# Revit family: FU_Inspec_Grade_2-3
name_source: partatom
category: Furniture
units: mm (PartAtom-declared; Revit-internal decimal feet)

## family parameters
Always vertical = Yes
Cut with Voids When Loaded = No
OmniClass Number = 23.40.20.00
OmniClass Title = General Furniture and Specialties
Room Calculation Point = No
Shared = No
Work Plane-Based = No

## types (3) — shared parameters
Assembly Code = E2020
Depth = 780 mm
Frame Material = Metal - Chrome - Polished
Height = 540 mm
Keynote = 46.B
Manufacturer = Inspec
Seat Material = Colour - Coated - White
URL = https://inspecfurniture.com
Weight = 5.0
Width = 570 mm
zero-valued in all types: Default Elevation

## per-type parameters (varying)
| type | Armrest Material | Description | Model | Seat Pad Material |
| Grade 2.1 - Chrome - White | Plastic - Black | Armchair with recycled polypropylene seat on a powder coated or chromium plated tubular steel frame. Stackable and linkable (armchair-chair-armchair) | Grade 2.1 | Fabric - Divina 3 - 236 |
| Grade 2.2 - Chrome - White | Plastic - White | Armchair with recycled polypropylene seat on a powder coated or chromium plated tubular steel frame, with upholstered seat pad. Stackable and linkable (armchair-chair-armchair) | Grade 2.2 | Fabric - Divina Black |
| Grade 2.3 - Chrome - White | Plastic - White | Armchair with fully upholstered recycled polypropylene seat on a powder coated or chromium plated tubular steel frame. Stackable and linkable (armchair-chair-armchair) | Grade 2.3 | Fabric - Divina Black |

## geometry (parser evidence)
native form markers: Blend x450, Sweep x2
no freeform markers — native parametric forms only
